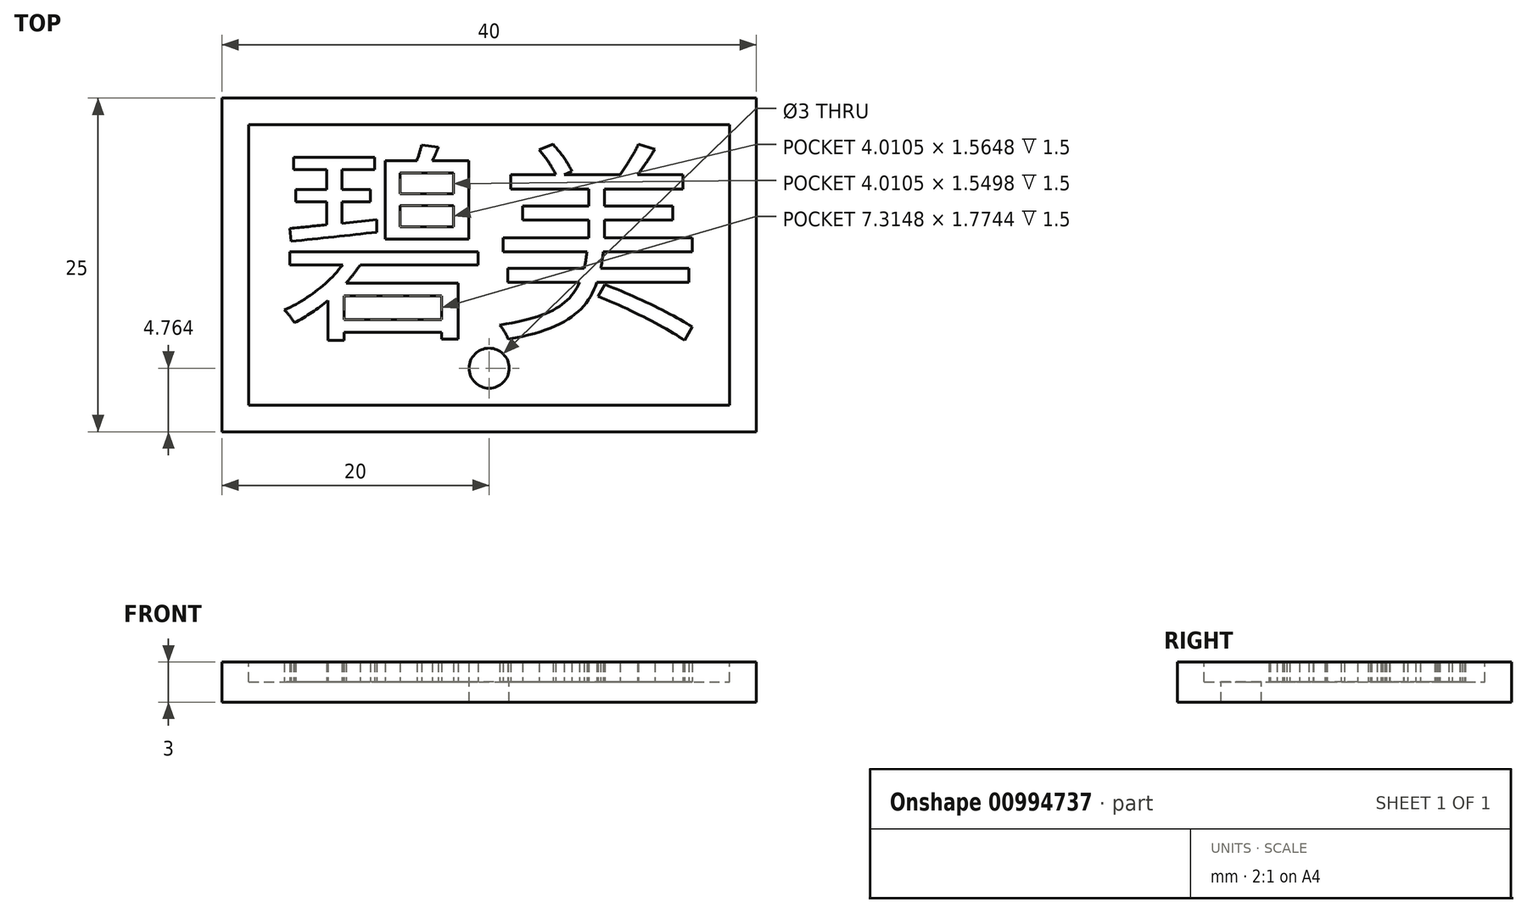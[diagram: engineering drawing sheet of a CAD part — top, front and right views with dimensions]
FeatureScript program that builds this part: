
annotation { "Feature Type Name" : "Feature", "Feature Type Description" : "" }
export const myFeature = defineFeature(function(context is Context, id is Id, definition is map)
    precondition{}
    {
        {
            var Q0;
            Q0=qCreatedBy(makeId("Top.planeOp"),FACE);
            var sketch = newSketch(context, id + "F0", { "sketchPlane" : qUnion([Q0])});
            skLineSegment(sketch, "E0.bottom", {"start": v(20, -12.5) * mm, "end": v(-20, -12.5) * mm});
            skLineSegment(sketch, "E0.top", {"start": v(20, 12.5) * mm, "end": v(-20, 12.5) * mm});
            skLineSegment(sketch, "E0.left", {"start": v(20, -12.5) * mm, "end": v(20, 12.5) * mm});
            skLineSegment(sketch, "E0.right", {"start": v(-20, -12.5) * mm, "end": v(-20, 12.5) * mm});
            skPoint(sketch, "E0.middle", {"position": v(0, 0) * mm});
            skSolve(sketch);
        }
        {
            var Q0;
            Q0 = qSketchRegion(id + "F0", true);
            extrude(context, id + "F1", {"entities" : qUnion([Q0]), "depth" : 3 * mm, "offsetDistance" : 25 * mm});
        }
        {
            var Q0;
            Q0=makeQuery(id+"F1.opExtrude","CAP_FACE",FACE,{"disambiguationData":[OSD([sQuery(id+"F0.wireOp",EDGE,"E0.bottom"),sQuery(id+"F0.wireOp",EDGE,"E0.top"),sQuery(id+"F0.wireOp",EDGE,"E0.left"),sQuery(id+"F0.wireOp",EDGE,"E0.right")])],"isStart":false});
            var sketch = newSketch(context, id + "F2", { "sketchPlane" : qUnion([Q0])});
            skLineSegment(sketch, "E1.0", {"start": v(18, -10.5) * mm, "end": v(18, 10.5) * mm});
            skLineSegment(sketch, "E1.1", {"start": v(-18, -10.5) * mm, "end": v(18, -10.5) * mm});
            skLineSegment(sketch, "E1.2", {"start": v(-18, 10.5) * mm, "end": v(-18, -10.5) * mm});
            skLineSegment(sketch, "E1.3", {"start": v(18, 10.5) * mm, "end": v(-18, 10.5) * mm});
            skSolve(sketch);
        }
        {
            var Q0;
            Q0 = qSketchRegion(id + "F2", true);
            extrude(context, id + "F3", {"entities" : qUnion([Q0]), "operationType" : NewBodyOperationType.REMOVE, "oppositeDirection" : true, "depth" : 1.5 * mm, "offsetDistance" : 25 * mm});
        }
        {
            var Q0;
            Q0=makeQuery(id+"F3.boolean.opBoolean","COPY",FACE,{"derivedFrom":makeQuery(id+"F3.opExtrude","CAP_FACE",FACE,{"disambiguationData":[OSD([sQuery(id+"F2.wireOp",EDGE,"E1.0"),sQuery(id+"F2.wireOp",EDGE,"E1.1"),sQuery(id+"F2.wireOp",EDGE,"E1.2"),sQuery(id+"F2.wireOp",EDGE,"E1.3")])],"isStart":false})});
            var sketch = newSketch(context, id + "F4", { "sketchPlane" : qUnion([Q0])});
            skCircle(sketch, "E2", {"center": v(0, -7.74) * mm, "radius": 1.5 * mm});
            skSolve(sketch);
        }
        {
            var Q0;
            Q0 = qSketchRegion(id + "F4", true);
            extrude(context, id + "F5", {"entities" : qUnion([Q0]), "operationType" : NewBodyOperationType.REMOVE, "endBound" : BoundingType.THROUGH_ALL, "oppositeDirection" : true, "depth" : 25 * mm, "offsetDistance" : 25 * mm});
        }
        {
            var Q0;
            Q0=makeQuery(id+"F3.boolean.opBoolean","COPY",FACE,{"derivedFrom":makeQuery(id+"F3.opExtrude","CAP_FACE",FACE,{"disambiguationData":[OSD([sQuery(id+"F2.wireOp",EDGE,"E1.0"),sQuery(id+"F2.wireOp",EDGE,"E1.1"),sQuery(id+"F2.wireOp",EDGE,"E1.2"),sQuery(id+"F2.wireOp",EDGE,"E1.3")])],"isStart":false})});
            var sketch = newSketch(context, id + "F6", { "sketchPlane" : qUnion([Q0])});
            skText(sketch, "E3", { "text": "碧美", "fontName": "NotoSansCJKtc-Regular.otf"});
            const initialGuessF6  = {"E3": [-0.01587, -0.00438, 1, 0, 0.0115]};
            skSetInitialGuess(sketch, initialGuessF6);
            skSolve(sketch);
        }
        {
            var Q0;
            Q0 = qSketchRegion(id + "F6", true);
            extrude(context, id + "F7", {"entities" : qUnion([Q0]), "operationType" : NewBodyOperationType.ADD, "depth" : 1.5 * mm, "offsetDistance" : 25 * mm});
        }
    });
